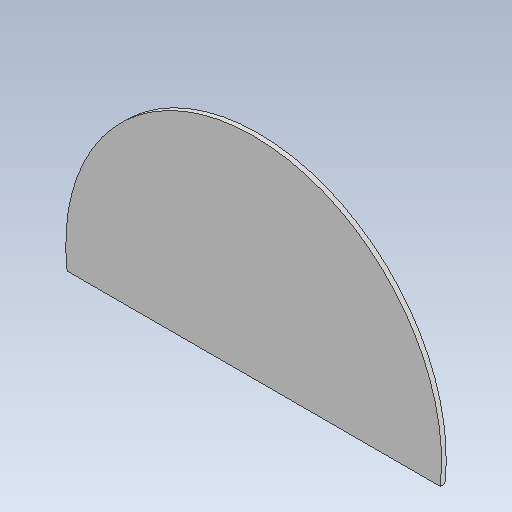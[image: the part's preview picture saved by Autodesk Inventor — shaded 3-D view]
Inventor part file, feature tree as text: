
AUTODESK INVENTOR PART (.ipt)
format: ipt  version: 2021 (Build 250183000, 183)  size: 96,256 bytes
history: native  units: mm
features: extrude x1, sketch x1
ambient origin geometry x8: Origin, YZ Plane, XZ Plane, XY Plane, X Axis, Y Axis, Z Axis, Center Point
bodies: Body1 (feature_tree)
feature tree (2):
  extrude  "side"  TaperAngle=0.0deg  [1 undecoded]
  sketch  "Sketch2"  dims[d14=20.0mm d15=0.0mm d17=0.0mm d21=0.0mm d24=890.0mm d25=1580.0mm d26=790.0mm]
note: 1 required parameter value undecoded (feature->parameter linkage not recoverable at this tier; creation-order binding heuristic only, values carry confidence <= 0.55)
